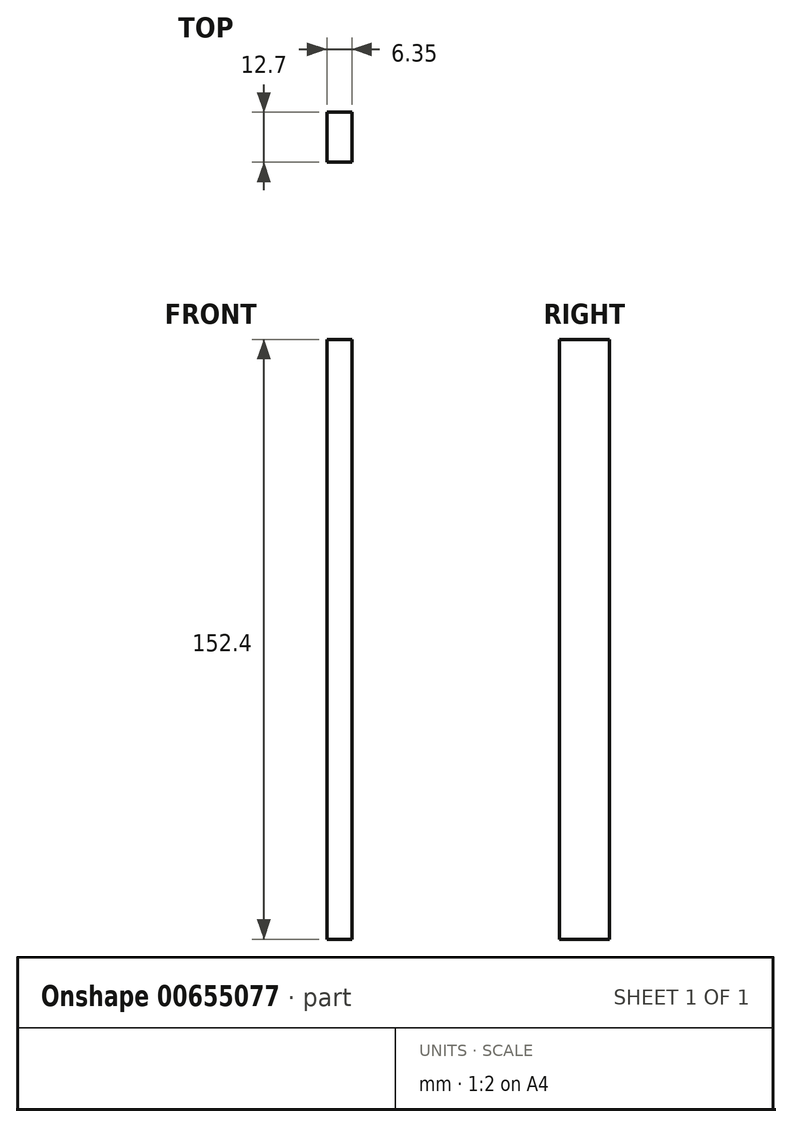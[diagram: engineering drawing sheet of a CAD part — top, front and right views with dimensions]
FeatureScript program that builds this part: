
annotation { "Feature Type Name" : "Feature", "Feature Type Description" : "" }
export const myFeature = defineFeature(function(context is Context, id is Id, definition is map)
    precondition{}
    {
        {
            var Q0;
            Q0=qCreatedBy(makeId("Right.planeOp"),FACE);
            var sketch = newSketch(context, id + "F0", { "sketchPlane" : qUnion([Q0])});
            skLineSegment(sketch, "E0.bottom", {"start": v(6.35, 76.2) * mm, "end": v(-6.35, 76.2) * mm});
            skLineSegment(sketch, "E0.top", {"start": v(6.35, -76.2) * mm, "end": v(-6.35, -76.2) * mm});
            skLineSegment(sketch, "E0.left", {"start": v(6.35, 76.2) * mm, "end": v(6.35, -76.2) * mm});
            skLineSegment(sketch, "E0.right", {"start": v(-6.35, 76.2) * mm, "end": v(-6.35, -76.2) * mm});
            skPoint(sketch, "E0.middle", {"position": v(0, 0) * mm});
            skSolve(sketch);
        }
        {
            var Q0;
            Q0 = qSketchRegion(id + "F0", true);
            extrude(context, id + "F1", {"entities" : qUnion([Q0]), "depth" : 6.35 * mm, "offsetDistance" : 25.4 * mm});
        }
    });
